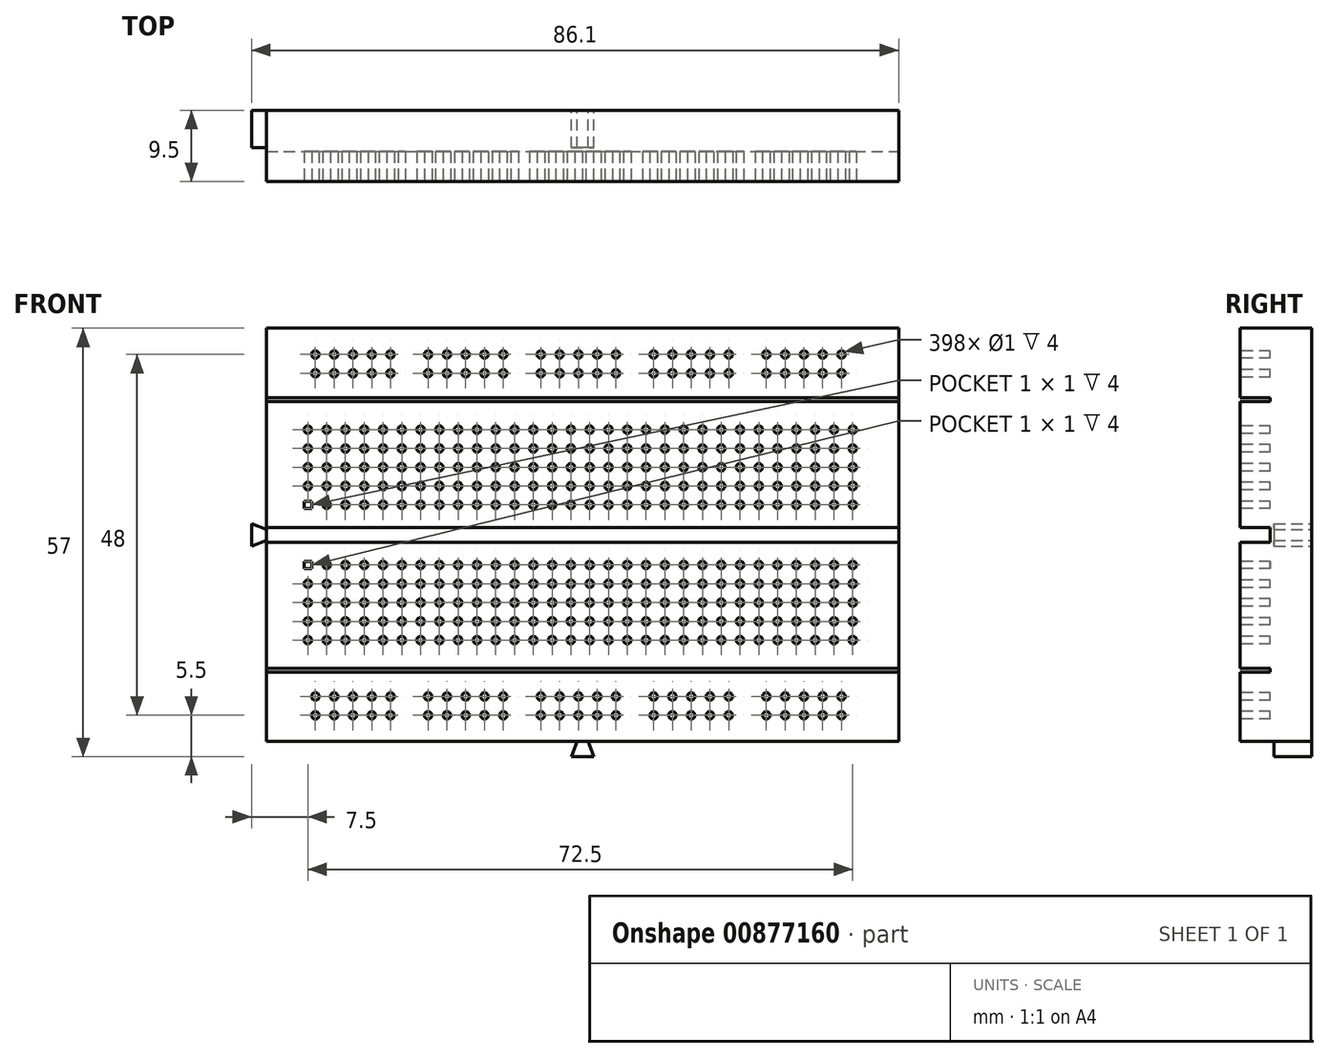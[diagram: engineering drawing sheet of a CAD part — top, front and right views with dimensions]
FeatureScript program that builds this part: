
annotation { "Feature Type Name" : "Feature", "Feature Type Description" : "" }
export const myFeature = defineFeature(function(context is Context, id is Id, definition is map)
    precondition{}
    {
        {
            var Q0;
            Q0=qCreatedBy(makeId("Front.planeOp"),FACE);
            var sketch = newSketch(context, id + "F0", { "sketchPlane" : qUnion([Q0])});
            skLineSegment(sketch, "E0.bottom", {"start": v(42.05, 27.5) * mm, "end": v(-42.05, 27.5) * mm});
            skLineSegment(sketch, "E0.top", {"start": v(42.05, -27.5) * mm, "end": v(-42.05, -27.5) * mm});
            skLineSegment(sketch, "E0.left", {"start": v(42.05, 27.5) * mm, "end": v(42.05, -27.5) * mm});
            skLineSegment(sketch, "E0.right", {"start": v(-42.05, 27.5) * mm, "end": v(-42.05, -27.5) * mm});
            skPoint(sketch, "E0.middle", {"position": v(0, 0) * mm});
            skSolve(sketch);
        }
        {
            var Q0;
            Q0 = qSketchRegion(id + "F0", true);
            extrude(context, id + "F1", {"entities" : qUnion([Q0]), "depth" : 9.5 * mm, "offsetDistance" : 25 * mm});
        }
        {
            var Q0;
            Q0=makeQuery(id+"F1.opExtrude","CAP_FACE",FACE,{"disambiguationData":[OSD([sQuery(id+"F0.wireOp",EDGE,"E0.bottom"),sQuery(id+"F0.wireOp",EDGE,"E0.top"),sQuery(id+"F0.wireOp",EDGE,"E0.left"),sQuery(id+"F0.wireOp",EDGE,"E0.right")])],"isStart":true});
            var sketch = newSketch(context, id + "F2", { "sketchPlane" : qUnion([Q0])});
            skLineSegment(sketch, "E1", {"start": v(42.05, 0.75) * mm, "end": v(44.05, 1.5) * mm});
            skLineSegment(sketch, "E2", {"start": v(44.05, 1.5) * mm, "end": v(44.05, -1.5) * mm});
            skLineSegment(sketch, "E3", {"start": v(44.05, -1.5) * mm, "end": v(42.05, -0.75) * mm});
            skLineSegment(sketch, "E4", {"start": v(0.75, -27.5) * mm, "end": v(1.5, -29.5) * mm});
            skLineSegment(sketch, "E5", {"start": v(1.5, -29.5) * mm, "end": v(-1.5, -29.5) * mm});
            skLineSegment(sketch, "E6", {"start": v(-1.5, -29.5) * mm, "end": v(-0.75, -27.5) * mm});
            skLineSegment(sketch, "E7", {"start": v(42.05, 0) * mm, "end": v(44.05, 0) * mm});
            skLineSegment(sketch, "E8", {"start": v(42.05, 0.75) * mm, "end": v(42.05, -0.75) * mm});
            skLineSegment(sketch, "E9", {"start": v(0.75, -27.5) * mm, "end": v(-0.75, -27.5) * mm});
            skLineSegment(sketch, "E10", {"start": v(0, -27.5) * mm, "end": v(0, -29.5) * mm, "construction": true});
            skSolve(sketch);
        }
        {
            var Q0;
            {var subQ0=sQuery(id+"F2.wireOp",EDGE,"E3");Q0=makeQuery(id+"F2.imprint","IMPRINT",FACE,{"disambiguationData":[TD([[makeQuery(id+"F2.imprint","IMPRINT",EDGE,{"derivedFrom":subQ0}),-1.0]])]});}
            var Q1;
            {var subQ0=sQuery(id+"F2.wireOp",EDGE,"E1");Q1=makeQuery(id+"F2.imprint","IMPRINT",FACE,{"disambiguationData":[TD([[makeQuery(id+"F2.imprint","IMPRINT",EDGE,{"derivedFrom":subQ0}),-1.0]])]});}
            var Q2;
            Q2=makeQuery(id+"F2.imprint","IMPRINT",FACE,{"disambiguationData":[TD([[makeQuery(id+"F2.imprint","IMPRINT",EDGE,{"derivedFrom":sQuery(id+"F2.wireOp",EDGE,"E4")}),-1.0]])]});
            extrude(context, id + "F3", {"entities" : qUnion([Q0, Q1, Q2]), "operationType" : NewBodyOperationType.ADD, "oppositeDirection" : true, "depth" : 5 * mm, "offsetDistance" : 25 * mm});
        }
        {
            var Q0;
            Q0=makeQuery(id+"F1.opExtrude","CAP_FACE",FACE,{"disambiguationData":[OSD([sQuery(id+"F0.wireOp",EDGE,"E0.bottom"),sQuery(id+"F0.wireOp",EDGE,"E0.top"),sQuery(id+"F0.wireOp",EDGE,"E0.left"),sQuery(id+"F0.wireOp",EDGE,"E0.right")])],"isStart":false});
            var sketch = newSketch(context, id + "F4", { "sketchPlane" : qUnion([Q0])});
            skSolve(sketch);
        }
        {
            var Q0;
            Q0=makeQuery(id+"F4.imprint","IMPRINT",FACE,{"disambiguationData":[TD([[makeQuery(id+"F4.imprint","IMPRINT",EDGE,{"derivedFrom":makeQuery(id+"F1.opExtrude","CAP_EDGE",EDGE,{"disambiguationData":[OSD([sQuery(id+"F0.wireOp",EDGE,"E0.bottom")])],"isStart":false})}),1.0]])]});
            var sketch = newSketch(context, id + "F5", { "sketchPlane" : qUnion([Q0])});
            skLineSegment(sketch, "E11.bottom", {"start": v(-42.05, -1) * mm, "end": v(42.05, -1) * mm});
            skLineSegment(sketch, "E11.top", {"start": v(-42.05, 1) * mm, "end": v(42.05, 1) * mm});
            skLineSegment(sketch, "E11.left", {"start": v(-42.05, -1) * mm, "end": v(-42.05, 1) * mm});
            skLineSegment(sketch, "E11.right", {"start": v(42.05, -1) * mm, "end": v(42.05, 1) * mm});
            skPoint(sketch, "E11.middle", {"position": v(0, 0) * mm});
            skLineSegment(sketch, "E12.bottom", {"start": v(-36.05, -3.5) * mm, "end": v(-37.05, -3.5) * mm});
            skLineSegment(sketch, "E12.top", {"start": v(-36.05, -4.5) * mm, "end": v(-37.05, -4.5) * mm});
            skLineSegment(sketch, "E12.left", {"start": v(-36.05, -3.5) * mm, "end": v(-36.05, -4.5) * mm});
            skLineSegment(sketch, "E12.right", {"start": v(-37.05, -3.5) * mm, "end": v(-37.05, -4.5) * mm});
            skPoint(sketch, "E12.middle", {"position": v(-36.55, -4) * mm});
            skCircle(sketch, "E13", {"center": v(-36.55, -4) * mm, "radius": 0.5 * mm});
            skCircle(sketch, "E14.1.0.0", {"center": v(-34.05, -4) * mm, "radius": 0.5 * mm});
            skCircle(sketch, "E14.2.0.0", {"center": v(-31.55, -4) * mm, "radius": 0.5 * mm});
            skCircle(sketch, "E14.3.0.0", {"center": v(-29.05, -4) * mm, "radius": 0.5 * mm});
            skCircle(sketch, "E14.4.0.0", {"center": v(-26.55, -4) * mm, "radius": 0.5 * mm});
            skCircle(sketch, "E14.5.0.0", {"center": v(-24.05, -4) * mm, "radius": 0.5 * mm});
            skCircle(sketch, "E14.6.0.0", {"center": v(-21.55, -4) * mm, "radius": 0.5 * mm});
            skCircle(sketch, "E14.7.0.0", {"center": v(-19.05, -4) * mm, "radius": 0.5 * mm});
            skCircle(sketch, "E14.8.0.0", {"center": v(-16.55, -4) * mm, "radius": 0.5 * mm});
            skCircle(sketch, "E14.9.0.0", {"center": v(-14.05, -4) * mm, "radius": 0.5 * mm});
            skCircle(sketch, "E14.10.0.0", {"center": v(-11.55, -4) * mm, "radius": 0.5 * mm});
            skCircle(sketch, "E14.11.0.0", {"center": v(-9.05, -4) * mm, "radius": 0.5 * mm});
            skCircle(sketch, "E14.12.0.0", {"center": v(-6.55, -4) * mm, "radius": 0.5 * mm});
            skCircle(sketch, "E14.13.0.0", {"center": v(-4.05, -4) * mm, "radius": 0.5 * mm});
            skCircle(sketch, "E14.14.0.0", {"center": v(-1.55, -4) * mm, "radius": 0.5 * mm});
            skCircle(sketch, "E14.15.0.0", {"center": v(0.95, -4) * mm, "radius": 0.5 * mm});
            skCircle(sketch, "E14.16.0.0", {"center": v(3.45, -4) * mm, "radius": 0.5 * mm});
            skCircle(sketch, "E14.17.0.0", {"center": v(5.95, -4) * mm, "radius": 0.5 * mm});
            skCircle(sketch, "E14.18.0.0", {"center": v(8.45, -4) * mm, "radius": 0.5 * mm});
            skCircle(sketch, "E14.19.0.0", {"center": v(10.95, -4) * mm, "radius": 0.5 * mm});
            skCircle(sketch, "E14.20.0.0", {"center": v(13.45, -4) * mm, "radius": 0.5 * mm});
            skCircle(sketch, "E14.21.0.0", {"center": v(15.95, -4) * mm, "radius": 0.5 * mm});
            skCircle(sketch, "E14.22.0.0", {"center": v(18.45, -4) * mm, "radius": 0.5 * mm});
            skCircle(sketch, "E14.23.0.0", {"center": v(20.95, -4) * mm, "radius": 0.5 * mm});
            skCircle(sketch, "E14.24.0.0", {"center": v(23.45, -4) * mm, "radius": 0.5 * mm});
            skCircle(sketch, "E14.25.0.0", {"center": v(25.95, -4) * mm, "radius": 0.5 * mm});
            skCircle(sketch, "E14.26.0.0", {"center": v(28.45, -4) * mm, "radius": 0.5 * mm});
            skCircle(sketch, "E14.27.0.0", {"center": v(30.95, -4) * mm, "radius": 0.5 * mm});
            skCircle(sketch, "E14.28.0.0", {"center": v(33.45, -4) * mm, "radius": 0.5 * mm});
            skCircle(sketch, "E14.29.0.0", {"center": v(35.95, -4) * mm, "radius": 0.5 * mm});
            skLineSegment(sketch, "E14.direction1", {"start": v(-36.55, -4) * mm, "end": v(-34.05, -4) * mm, "construction": true});
            skPoint(sketch, "E15.0.1.0", {"position": v(-36.55, -6.5) * mm});
            skCircle(sketch, "E15.0.1.1", {"center": v(25.95, -6.5) * mm, "radius": 0.5 * mm});
            skCircle(sketch, "E15.0.1.2", {"center": v(28.45, -6.5) * mm, "radius": 0.5 * mm});
            skCircle(sketch, "E15.0.1.3", {"center": v(-16.55, -6.5) * mm, "radius": 0.5 * mm});
            skCircle(sketch, "E15.0.1.4", {"center": v(5.95, -6.5) * mm, "radius": 0.5 * mm});
            skCircle(sketch, "E15.0.1.5", {"center": v(-31.55, -6.5) * mm, "radius": 0.5 * mm});
            skCircle(sketch, "E15.0.1.6", {"center": v(20.95, -6.5) * mm, "radius": 0.5 * mm});
            skCircle(sketch, "E15.0.1.7", {"center": v(-9.05, -6.5) * mm, "radius": 0.5 * mm});
            skCircle(sketch, "E15.0.1.8", {"center": v(10.95, -6.5) * mm, "radius": 0.5 * mm});
            skCircle(sketch, "E15.0.1.9", {"center": v(0.95, -6.5) * mm, "radius": 0.5 * mm});
            skCircle(sketch, "E15.0.1.10", {"center": v(8.45, -6.5) * mm, "radius": 0.5 * mm});
            skCircle(sketch, "E15.0.1.11", {"center": v(-14.05, -6.5) * mm, "radius": 0.5 * mm});
            skCircle(sketch, "E15.0.1.12", {"center": v(-4.05, -6.5) * mm, "radius": 0.5 * mm});
            skCircle(sketch, "E15.0.1.13", {"center": v(-11.55, -6.5) * mm, "radius": 0.5 * mm});
            skCircle(sketch, "E15.0.1.14", {"center": v(15.95, -6.5) * mm, "radius": 0.5 * mm});
            skCircle(sketch, "E15.0.1.15", {"center": v(3.45, -6.5) * mm, "radius": 0.5 * mm});
            skCircle(sketch, "E15.0.1.16", {"center": v(13.45, -6.5) * mm, "radius": 0.5 * mm});
            skCircle(sketch, "E15.0.1.17", {"center": v(-6.55, -6.5) * mm, "radius": 0.5 * mm});
            skCircle(sketch, "E15.0.1.18", {"center": v(-29.05, -6.5) * mm, "radius": 0.5 * mm});
            skCircle(sketch, "E15.0.1.19", {"center": v(18.45, -6.5) * mm, "radius": 0.5 * mm});
            skCircle(sketch, "E15.0.1.20", {"center": v(23.45, -6.5) * mm, "radius": 0.5 * mm});
            skCircle(sketch, "E15.0.1.21", {"center": v(30.95, -6.5) * mm, "radius": 0.5 * mm});
            skCircle(sketch, "E15.0.1.22", {"center": v(33.45, -6.5) * mm, "radius": 0.5 * mm});
            skCircle(sketch, "E15.0.1.23", {"center": v(-21.55, -6.5) * mm, "radius": 0.5 * mm});
            skCircle(sketch, "E15.0.1.24", {"center": v(-26.55, -6.5) * mm, "radius": 0.5 * mm});
            skCircle(sketch, "E15.0.1.25", {"center": v(-24.05, -6.5) * mm, "radius": 0.5 * mm});
            skCircle(sketch, "E15.0.1.26", {"center": v(-19.05, -6.5) * mm, "radius": 0.5 * mm});
            skCircle(sketch, "E15.0.1.27", {"center": v(35.95, -6.5) * mm, "radius": 0.5 * mm});
            skCircle(sketch, "E15.0.1.28", {"center": v(-1.55, -6.5) * mm, "radius": 0.5 * mm});
            skCircle(sketch, "E15.0.1.29", {"center": v(-34.05, -6.5) * mm, "radius": 0.5 * mm});
            skCircle(sketch, "E15.0.1.30", {"center": v(-36.55, -6.5) * mm, "radius": 0.5 * mm});
            skPoint(sketch, "E15.0.2.0", {"position": v(-36.55, -9) * mm});
            skCircle(sketch, "E15.0.2.1", {"center": v(25.95, -9) * mm, "radius": 0.5 * mm});
            skCircle(sketch, "E15.0.2.2", {"center": v(28.45, -9) * mm, "radius": 0.5 * mm});
            skCircle(sketch, "E15.0.2.3", {"center": v(-16.55, -9) * mm, "radius": 0.5 * mm});
            skCircle(sketch, "E15.0.2.4", {"center": v(5.95, -9) * mm, "radius": 0.5 * mm});
            skCircle(sketch, "E15.0.2.5", {"center": v(-31.55, -9) * mm, "radius": 0.5 * mm});
            skCircle(sketch, "E15.0.2.6", {"center": v(20.95, -9) * mm, "radius": 0.5 * mm});
            skCircle(sketch, "E15.0.2.7", {"center": v(-9.05, -9) * mm, "radius": 0.5 * mm});
            skCircle(sketch, "E15.0.2.8", {"center": v(10.95, -9) * mm, "radius": 0.5 * mm});
            skCircle(sketch, "E15.0.2.9", {"center": v(0.95, -9) * mm, "radius": 0.5 * mm});
            skCircle(sketch, "E15.0.2.10", {"center": v(8.45, -9) * mm, "radius": 0.5 * mm});
            skCircle(sketch, "E15.0.2.11", {"center": v(-14.05, -9) * mm, "radius": 0.5 * mm});
            skCircle(sketch, "E15.0.2.12", {"center": v(-4.05, -9) * mm, "radius": 0.5 * mm});
            skCircle(sketch, "E15.0.2.13", {"center": v(-11.55, -9) * mm, "radius": 0.5 * mm});
            skCircle(sketch, "E15.0.2.14", {"center": v(15.95, -9) * mm, "radius": 0.5 * mm});
            skCircle(sketch, "E15.0.2.15", {"center": v(3.45, -9) * mm, "radius": 0.5 * mm});
            skCircle(sketch, "E15.0.2.16", {"center": v(13.45, -9) * mm, "radius": 0.5 * mm});
            skCircle(sketch, "E15.0.2.17", {"center": v(-6.55, -9) * mm, "radius": 0.5 * mm});
            skCircle(sketch, "E15.0.2.18", {"center": v(-29.05, -9) * mm, "radius": 0.5 * mm});
            skCircle(sketch, "E15.0.2.19", {"center": v(18.45, -9) * mm, "radius": 0.5 * mm});
            skCircle(sketch, "E15.0.2.20", {"center": v(23.45, -9) * mm, "radius": 0.5 * mm});
            skCircle(sketch, "E15.0.2.21", {"center": v(30.95, -9) * mm, "radius": 0.5 * mm});
            skCircle(sketch, "E15.0.2.22", {"center": v(33.45, -9) * mm, "radius": 0.5 * mm});
            skCircle(sketch, "E15.0.2.23", {"center": v(-21.55, -9) * mm, "radius": 0.5 * mm});
            skCircle(sketch, "E15.0.2.24", {"center": v(-26.55, -9) * mm, "radius": 0.5 * mm});
            skCircle(sketch, "E15.0.2.25", {"center": v(-24.05, -9) * mm, "radius": 0.5 * mm});
            skCircle(sketch, "E15.0.2.26", {"center": v(-19.05, -9) * mm, "radius": 0.5 * mm});
            skCircle(sketch, "E15.0.2.27", {"center": v(35.95, -9) * mm, "radius": 0.5 * mm});
            skCircle(sketch, "E15.0.2.28", {"center": v(-1.55, -9) * mm, "radius": 0.5 * mm});
            skCircle(sketch, "E15.0.2.29", {"center": v(-34.05, -9) * mm, "radius": 0.5 * mm});
            skCircle(sketch, "E15.0.2.30", {"center": v(-36.55, -9) * mm, "radius": 0.5 * mm});
            skPoint(sketch, "E15.0.3.0", {"position": v(-36.55, -11.5) * mm});
            skCircle(sketch, "E15.0.3.1", {"center": v(25.95, -11.5) * mm, "radius": 0.5 * mm});
            skCircle(sketch, "E15.0.3.2", {"center": v(28.45, -11.5) * mm, "radius": 0.5 * mm});
            skCircle(sketch, "E15.0.3.3", {"center": v(-16.55, -11.5) * mm, "radius": 0.5 * mm});
            skCircle(sketch, "E15.0.3.4", {"center": v(5.95, -11.5) * mm, "radius": 0.5 * mm});
            skCircle(sketch, "E15.0.3.5", {"center": v(-31.55, -11.5) * mm, "radius": 0.5 * mm});
            skCircle(sketch, "E15.0.3.6", {"center": v(20.95, -11.5) * mm, "radius": 0.5 * mm});
            skCircle(sketch, "E15.0.3.7", {"center": v(-9.05, -11.5) * mm, "radius": 0.5 * mm});
            skCircle(sketch, "E15.0.3.8", {"center": v(10.95, -11.5) * mm, "radius": 0.5 * mm});
            skCircle(sketch, "E15.0.3.9", {"center": v(0.95, -11.5) * mm, "radius": 0.5 * mm});
            skCircle(sketch, "E15.0.3.10", {"center": v(8.45, -11.5) * mm, "radius": 0.5 * mm});
            skCircle(sketch, "E15.0.3.11", {"center": v(-14.05, -11.5) * mm, "radius": 0.5 * mm});
            skCircle(sketch, "E15.0.3.12", {"center": v(-4.05, -11.5) * mm, "radius": 0.5 * mm});
            skCircle(sketch, "E15.0.3.13", {"center": v(-11.55, -11.5) * mm, "radius": 0.5 * mm});
            skCircle(sketch, "E15.0.3.14", {"center": v(15.95, -11.5) * mm, "radius": 0.5 * mm});
            skCircle(sketch, "E15.0.3.15", {"center": v(3.45, -11.5) * mm, "radius": 0.5 * mm});
            skCircle(sketch, "E15.0.3.16", {"center": v(13.45, -11.5) * mm, "radius": 0.5 * mm});
            skCircle(sketch, "E15.0.3.17", {"center": v(-6.55, -11.5) * mm, "radius": 0.5 * mm});
            skCircle(sketch, "E15.0.3.18", {"center": v(-29.05, -11.5) * mm, "radius": 0.5 * mm});
            skCircle(sketch, "E15.0.3.19", {"center": v(18.45, -11.5) * mm, "radius": 0.5 * mm});
            skCircle(sketch, "E15.0.3.20", {"center": v(23.45, -11.5) * mm, "radius": 0.5 * mm});
            skCircle(sketch, "E15.0.3.21", {"center": v(30.95, -11.5) * mm, "radius": 0.5 * mm});
            skCircle(sketch, "E15.0.3.22", {"center": v(33.45, -11.5) * mm, "radius": 0.5 * mm});
            skCircle(sketch, "E15.0.3.23", {"center": v(-21.55, -11.5) * mm, "radius": 0.5 * mm});
            skCircle(sketch, "E15.0.3.24", {"center": v(-26.55, -11.5) * mm, "radius": 0.5 * mm});
            skCircle(sketch, "E15.0.3.25", {"center": v(-24.05, -11.5) * mm, "radius": 0.5 * mm});
            skCircle(sketch, "E15.0.3.26", {"center": v(-19.05, -11.5) * mm, "radius": 0.5 * mm});
            skCircle(sketch, "E15.0.3.27", {"center": v(35.95, -11.5) * mm, "radius": 0.5 * mm});
            skCircle(sketch, "E15.0.3.28", {"center": v(-1.55, -11.5) * mm, "radius": 0.5 * mm});
            skCircle(sketch, "E15.0.3.29", {"center": v(-34.05, -11.5) * mm, "radius": 0.5 * mm});
            skCircle(sketch, "E15.0.3.30", {"center": v(-36.55, -11.5) * mm, "radius": 0.5 * mm});
            skPoint(sketch, "E15.0.4.0", {"position": v(-36.55, -14) * mm});
            skCircle(sketch, "E15.0.4.1", {"center": v(25.95, -14) * mm, "radius": 0.5 * mm});
            skCircle(sketch, "E15.0.4.2", {"center": v(28.45, -14) * mm, "radius": 0.5 * mm});
            skCircle(sketch, "E15.0.4.3", {"center": v(-16.55, -14) * mm, "radius": 0.5 * mm});
            skCircle(sketch, "E15.0.4.4", {"center": v(5.95, -14) * mm, "radius": 0.5 * mm});
            skCircle(sketch, "E15.0.4.5", {"center": v(-31.55, -14) * mm, "radius": 0.5 * mm});
            skCircle(sketch, "E15.0.4.6", {"center": v(20.95, -14) * mm, "radius": 0.5 * mm});
            skCircle(sketch, "E15.0.4.7", {"center": v(-9.05, -14) * mm, "radius": 0.5 * mm});
            skCircle(sketch, "E15.0.4.8", {"center": v(10.95, -14) * mm, "radius": 0.5 * mm});
            skCircle(sketch, "E15.0.4.9", {"center": v(0.95, -14) * mm, "radius": 0.5 * mm});
            skCircle(sketch, "E15.0.4.10", {"center": v(8.45, -14) * mm, "radius": 0.5 * mm});
            skCircle(sketch, "E15.0.4.11", {"center": v(-14.05, -14) * mm, "radius": 0.5 * mm});
            skCircle(sketch, "E15.0.4.12", {"center": v(-4.05, -14) * mm, "radius": 0.5 * mm});
            skCircle(sketch, "E15.0.4.13", {"center": v(-11.55, -14) * mm, "radius": 0.5 * mm});
            skCircle(sketch, "E15.0.4.14", {"center": v(15.95, -14) * mm, "radius": 0.5 * mm});
            skCircle(sketch, "E15.0.4.15", {"center": v(3.45, -14) * mm, "radius": 0.5 * mm});
            skCircle(sketch, "E15.0.4.16", {"center": v(13.45, -14) * mm, "radius": 0.5 * mm});
            skCircle(sketch, "E15.0.4.17", {"center": v(-6.55, -14) * mm, "radius": 0.5 * mm});
            skCircle(sketch, "E15.0.4.18", {"center": v(-29.05, -14) * mm, "radius": 0.5 * mm});
            skCircle(sketch, "E15.0.4.19", {"center": v(18.45, -14) * mm, "radius": 0.5 * mm});
            skCircle(sketch, "E15.0.4.20", {"center": v(23.45, -14) * mm, "radius": 0.5 * mm});
            skCircle(sketch, "E15.0.4.21", {"center": v(30.95, -14) * mm, "radius": 0.5 * mm});
            skCircle(sketch, "E15.0.4.22", {"center": v(33.45, -14) * mm, "radius": 0.5 * mm});
            skCircle(sketch, "E15.0.4.23", {"center": v(-21.55, -14) * mm, "radius": 0.5 * mm});
            skCircle(sketch, "E15.0.4.24", {"center": v(-26.55, -14) * mm, "radius": 0.5 * mm});
            skCircle(sketch, "E15.0.4.25", {"center": v(-24.05, -14) * mm, "radius": 0.5 * mm});
            skCircle(sketch, "E15.0.4.26", {"center": v(-19.05, -14) * mm, "radius": 0.5 * mm});
            skCircle(sketch, "E15.0.4.27", {"center": v(35.95, -14) * mm, "radius": 0.5 * mm});
            skCircle(sketch, "E15.0.4.28", {"center": v(-1.55, -14) * mm, "radius": 0.5 * mm});
            skCircle(sketch, "E15.0.4.29", {"center": v(-34.05, -14) * mm, "radius": 0.5 * mm});
            skCircle(sketch, "E15.0.4.30", {"center": v(-36.55, -14) * mm, "radius": 0.5 * mm});
            skLineSegment(sketch, "E15.direction1", {"start": v(-36.55, -4) * mm, "end": v(-11.55, -4) * mm, "construction": true});
            skLineSegment(sketch, "E15.direction2", {"start": v(-36.55, -4) * mm, "end": v(-36.55, -6.5) * mm, "construction": true});
            skLineSegment(sketch, "E16.bottom", {"start": v(-42.05, -17.75) * mm, "end": v(42.05, -17.75) * mm});
            skLineSegment(sketch, "E16.top", {"start": v(-42.05, -18.25) * mm, "end": v(42.05, -18.25) * mm});
            skLineSegment(sketch, "E16.left", {"start": v(-42.05, -17.75) * mm, "end": v(-42.05, -18.25) * mm});
            skLineSegment(sketch, "E16.right", {"start": v(42.05, -17.75) * mm, "end": v(42.05, -18.25) * mm});
            skCircle(sketch, "E17.0.4.30", {"center": v(-35.55, -21.5) * mm, "radius": 0.5 * mm});
            skCircle(sketch, "E18.0.1.0", {"center": v(-35.55, -24) * mm, "radius": 0.5 * mm});
            skCircle(sketch, "E18.1.0.0", {"center": v(-33.05, -21.5) * mm, "radius": 0.5 * mm});
            skCircle(sketch, "E18.1.1.0", {"center": v(-33.05, -24) * mm, "radius": 0.5 * mm});
            skCircle(sketch, "E18.2.0.0", {"center": v(-30.55, -21.5) * mm, "radius": 0.5 * mm});
            skCircle(sketch, "E18.2.1.0", {"center": v(-30.55, -24) * mm, "radius": 0.5 * mm});
            skCircle(sketch, "E18.3.0.0", {"center": v(-28.05, -21.5) * mm, "radius": 0.5 * mm});
            skCircle(sketch, "E18.3.1.0", {"center": v(-28.05, -24) * mm, "radius": 0.5 * mm});
            skCircle(sketch, "E18.4.0.0", {"center": v(-25.55, -21.5) * mm, "radius": 0.5 * mm});
            skCircle(sketch, "E18.4.1.0", {"center": v(-25.55, -24) * mm, "radius": 0.5 * mm});
            skLineSegment(sketch, "E18.direction1", {"start": v(-35.55, -21.5) * mm, "end": v(-33.05, -21.5) * mm, "construction": true});
            skLineSegment(sketch, "E18.direction2", {"start": v(-35.55, -21.5) * mm, "end": v(-35.55, -24) * mm, "construction": true});
            skCircle(sketch, "E19.1.0.0", {"center": v(-18.05, -24) * mm, "radius": 0.5 * mm});
            skCircle(sketch, "E19.1.0.1", {"center": v(-10.55, -24) * mm, "radius": 0.5 * mm});
            skCircle(sketch, "E19.1.0.2", {"center": v(-13.05, -21.5) * mm, "radius": 0.5 * mm});
            skCircle(sketch, "E19.1.0.3", {"center": v(-18.05, -21.5) * mm, "radius": 0.5 * mm});
            skCircle(sketch, "E19.1.0.4", {"center": v(-15.55, -21.5) * mm, "radius": 0.5 * mm});
            skLineSegment(sketch, "E19.1.0.5", {"start": v(-20.55, -21.5) * mm, "end": v(-18.05, -21.5) * mm, "construction": true});
            skLineSegment(sketch, "E19.1.0.6", {"start": v(-20.55, -21.5) * mm, "end": v(-20.55, -24) * mm, "construction": true});
            skCircle(sketch, "E19.1.0.7", {"center": v(-20.55, -24) * mm, "radius": 0.5 * mm});
            skCircle(sketch, "E19.1.0.8", {"center": v(-13.05, -24) * mm, "radius": 0.5 * mm});
            skCircle(sketch, "E19.1.0.9", {"center": v(-10.55, -21.5) * mm, "radius": 0.5 * mm});
            skCircle(sketch, "E19.1.0.10", {"center": v(-15.55, -24) * mm, "radius": 0.5 * mm});
            skCircle(sketch, "E19.1.0.11", {"center": v(-20.55, -21.5) * mm, "radius": 0.5 * mm});
            skCircle(sketch, "E19.2.0.0", {"center": v(-3.05, -24) * mm, "radius": 0.5 * mm});
            skCircle(sketch, "E19.2.0.1", {"center": v(4.45, -24) * mm, "radius": 0.5 * mm});
            skCircle(sketch, "E19.2.0.2", {"center": v(1.95, -21.5) * mm, "radius": 0.5 * mm});
            skCircle(sketch, "E19.2.0.3", {"center": v(-3.05, -21.5) * mm, "radius": 0.5 * mm});
            skCircle(sketch, "E19.2.0.4", {"center": v(-0.55, -21.5) * mm, "radius": 0.5 * mm});
            skLineSegment(sketch, "E19.2.0.5", {"start": v(-5.55, -21.5) * mm, "end": v(-3.05, -21.5) * mm, "construction": true});
            skLineSegment(sketch, "E19.2.0.6", {"start": v(-5.55, -21.5) * mm, "end": v(-5.55, -24) * mm, "construction": true});
            skCircle(sketch, "E19.2.0.7", {"center": v(-5.55, -24) * mm, "radius": 0.5 * mm});
            skCircle(sketch, "E19.2.0.8", {"center": v(1.95, -24) * mm, "radius": 0.5 * mm});
            skCircle(sketch, "E19.2.0.9", {"center": v(4.45, -21.5) * mm, "radius": 0.5 * mm});
            skCircle(sketch, "E19.2.0.10", {"center": v(-0.55, -24) * mm, "radius": 0.5 * mm});
            skCircle(sketch, "E19.2.0.11", {"center": v(-5.55, -21.5) * mm, "radius": 0.5 * mm});
            skCircle(sketch, "E19.3.0.0", {"center": v(11.95, -24) * mm, "radius": 0.5 * mm});
            skCircle(sketch, "E19.3.0.1", {"center": v(19.45, -24) * mm, "radius": 0.5 * mm});
            skCircle(sketch, "E19.3.0.2", {"center": v(16.95, -21.5) * mm, "radius": 0.5 * mm});
            skCircle(sketch, "E19.3.0.3", {"center": v(11.95, -21.5) * mm, "radius": 0.5 * mm});
            skCircle(sketch, "E19.3.0.4", {"center": v(14.45, -21.5) * mm, "radius": 0.5 * mm});
            skLineSegment(sketch, "E19.3.0.5", {"start": v(9.45, -21.5) * mm, "end": v(11.95, -21.5) * mm, "construction": true});
            skLineSegment(sketch, "E19.3.0.6", {"start": v(9.45, -21.5) * mm, "end": v(9.45, -24) * mm, "construction": true});
            skCircle(sketch, "E19.3.0.7", {"center": v(9.45, -24) * mm, "radius": 0.5 * mm});
            skCircle(sketch, "E19.3.0.8", {"center": v(16.95, -24) * mm, "radius": 0.5 * mm});
            skCircle(sketch, "E19.3.0.9", {"center": v(19.45, -21.5) * mm, "radius": 0.5 * mm});
            skCircle(sketch, "E19.3.0.10", {"center": v(14.45, -24) * mm, "radius": 0.5 * mm});
            skCircle(sketch, "E19.3.0.11", {"center": v(9.45, -21.5) * mm, "radius": 0.5 * mm});
            skCircle(sketch, "E19.4.0.0", {"center": v(26.95, -24) * mm, "radius": 0.5 * mm});
            skCircle(sketch, "E19.4.0.1", {"center": v(34.45, -24) * mm, "radius": 0.5 * mm});
            skCircle(sketch, "E19.4.0.2", {"center": v(31.95, -21.5) * mm, "radius": 0.5 * mm});
            skCircle(sketch, "E19.4.0.3", {"center": v(26.95, -21.5) * mm, "radius": 0.5 * mm});
            skCircle(sketch, "E19.4.0.4", {"center": v(29.45, -21.5) * mm, "radius": 0.5 * mm});
            skLineSegment(sketch, "E19.4.0.5", {"start": v(24.45, -21.5) * mm, "end": v(26.95, -21.5) * mm, "construction": true});
            skLineSegment(sketch, "E19.4.0.6", {"start": v(24.45, -21.5) * mm, "end": v(24.45, -24) * mm, "construction": true});
            skCircle(sketch, "E19.4.0.7", {"center": v(24.45, -24) * mm, "radius": 0.5 * mm});
            skCircle(sketch, "E19.4.0.8", {"center": v(31.95, -24) * mm, "radius": 0.5 * mm});
            skCircle(sketch, "E19.4.0.9", {"center": v(34.45, -21.5) * mm, "radius": 0.5 * mm});
            skCircle(sketch, "E19.4.0.10", {"center": v(29.45, -24) * mm, "radius": 0.5 * mm});
            skCircle(sketch, "E19.4.0.11", {"center": v(24.45, -21.5) * mm, "radius": 0.5 * mm});
            skLineSegment(sketch, "E19.direction1", {"start": v(-35.55, -24) * mm, "end": v(-20.55, -24) * mm, "construction": true});
            skLineSegment(sketch, "E20.MirrorCS", {"start": v(-36.05, 3.5) * mm, "end": v(-37.05, 3.5) * mm});
            skLineSegment(sketch, "E21.MirrorCS", {"start": v(-37.05, 3.5) * mm, "end": v(-37.05, 4.5) * mm});
            skLineSegment(sketch, "E22.MirrorCS", {"start": v(-36.05, 3.5) * mm, "end": v(-36.05, 4.5) * mm});
            skLineSegment(sketch, "E23.MirrorCS", {"start": v(-36.05, 4.5) * mm, "end": v(-37.05, 4.5) * mm});
            skCircle(sketch, "E24.MirrorC", {"center": v(-36.55, 4) * mm, "radius": 0.5 * mm});
            skLineSegment(sketch, "E25.MirrorCS", {"start": v(-36.55, 4) * mm, "end": v(-36.55, 6.5) * mm, "construction": true});
            skCircle(sketch, "E26.MirrorC", {"center": v(-35.55, 21.5) * mm, "radius": 0.5 * mm});
            skCircle(sketch, "E27.MirrorC", {"center": v(24.45, 21.5) * mm, "radius": 0.5 * mm});
            skCircle(sketch, "E28.MirrorC", {"center": v(-20.55, 21.5) * mm, "radius": 0.5 * mm});
            skCircle(sketch, "E29.MirrorC", {"center": v(-36.55, 6.5) * mm, "radius": 0.5 * mm});
            skCircle(sketch, "E30.MirrorC", {"center": v(-5.55, 21.5) * mm, "radius": 0.5 * mm});
            skCircle(sketch, "E31.MirrorC", {"center": v(9.45, 21.5) * mm, "radius": 0.5 * mm});
            skCircle(sketch, "E32.MirrorC", {"center": v(-20.55, 24) * mm, "radius": 0.5 * mm});
            skCircle(sketch, "E33.MirrorC", {"center": v(-35.55, 24) * mm, "radius": 0.5 * mm});
            skLineSegment(sketch, "E34.MirrorCS", {"start": v(-36.55, 4) * mm, "end": v(-34.05, 4) * mm, "construction": true});
            skCircle(sketch, "E35.MirrorC", {"center": v(-36.55, 11.5) * mm, "radius": 0.5 * mm});
            skCircle(sketch, "E36.MirrorC", {"center": v(-3.05, 21.5) * mm, "radius": 0.5 * mm});
            skCircle(sketch, "E37.MirrorC", {"center": v(-5.55, 24) * mm, "radius": 0.5 * mm});
            skCircle(sketch, "E38.MirrorC", {"center": v(-36.55, 9) * mm, "radius": 0.5 * mm});
            skCircle(sketch, "E39.MirrorC", {"center": v(26.95, 21.5) * mm, "radius": 0.5 * mm});
            skCircle(sketch, "E40.MirrorC", {"center": v(-11.55, 4) * mm, "radius": 0.5 * mm});
            skLineSegment(sketch, "E41.MirrorCS", {"start": v(42.05, 17.75) * mm, "end": v(42.05, 18.25) * mm});
            skCircle(sketch, "E42.MirrorC", {"center": v(11.95, 21.5) * mm, "radius": 0.5 * mm});
            skCircle(sketch, "E43.MirrorC", {"center": v(-18.05, 21.5) * mm, "radius": 0.5 * mm});
            skCircle(sketch, "E44.MirrorC", {"center": v(-34.05, 4) * mm, "radius": 0.5 * mm});
            skLineSegment(sketch, "E45.MirrorCS", {"start": v(-42.05, 17.75) * mm, "end": v(-42.05, 18.25) * mm});
            skCircle(sketch, "E46.MirrorC", {"center": v(-36.55, 14) * mm, "radius": 0.5 * mm});
            skCircle(sketch, "E47.MirrorC", {"center": v(9.45, 24) * mm, "radius": 0.5 * mm});
            skCircle(sketch, "E48.MirrorC", {"center": v(24.45, 24) * mm, "radius": 0.5 * mm});
            skCircle(sketch, "E49.MirrorC", {"center": v(-33.05, 21.5) * mm, "radius": 0.5 * mm});
            skCircle(sketch, "E50.MirrorC", {"center": v(-18.05, 24) * mm, "radius": 0.5 * mm});
            skCircle(sketch, "E51.MirrorC", {"center": v(3.45, 4) * mm, "radius": 0.5 * mm});
            skCircle(sketch, "E52.MirrorC", {"center": v(-26.55, 9) * mm, "radius": 0.5 * mm});
            skCircle(sketch, "E53.MirrorC", {"center": v(20.95, 11.5) * mm, "radius": 0.5 * mm});
            skCircle(sketch, "E54.MirrorC", {"center": v(-26.55, 6.5) * mm, "radius": 0.5 * mm});
            skCircle(sketch, "E55.MirrorC", {"center": v(-29.05, 6.5) * mm, "radius": 0.5 * mm});
            skCircle(sketch, "E56.MirrorC", {"center": v(25.95, 11.5) * mm, "radius": 0.5 * mm});
            skCircle(sketch, "E57.MirrorC", {"center": v(30.95, 9) * mm, "radius": 0.5 * mm});
            skCircle(sketch, "E58.MirrorC", {"center": v(-10.55, 24) * mm, "radius": 0.5 * mm});
            skCircle(sketch, "E59.MirrorC", {"center": v(-21.55, 9) * mm, "radius": 0.5 * mm});
            skCircle(sketch, "E60.MirrorC", {"center": v(35.95, 9) * mm, "radius": 0.5 * mm});
            skCircle(sketch, "E61.MirrorC", {"center": v(-21.55, 14) * mm, "radius": 0.5 * mm});
            skCircle(sketch, "E62.MirrorC", {"center": v(16.95, 21.5) * mm, "radius": 0.5 * mm});
            skCircle(sketch, "E63.MirrorC", {"center": v(30.95, 4) * mm, "radius": 0.5 * mm});
            skCircle(sketch, "E64.MirrorC", {"center": v(-11.55, 6.5) * mm, "radius": 0.5 * mm});
            skCircle(sketch, "E65.MirrorC", {"center": v(-19.05, 6.5) * mm, "radius": 0.5 * mm});
            skCircle(sketch, "E66.MirrorC", {"center": v(-9.05, 4) * mm, "radius": 0.5 * mm});
            skCircle(sketch, "E67.MirrorC", {"center": v(25.95, 9) * mm, "radius": 0.5 * mm});
            skCircle(sketch, "E68.MirrorC", {"center": v(-28.05, 24) * mm, "radius": 0.5 * mm});
            skCircle(sketch, "E69.MirrorC", {"center": v(-31.55, 14) * mm, "radius": 0.5 * mm});
            skCircle(sketch, "E70.MirrorC", {"center": v(-19.05, 14) * mm, "radius": 0.5 * mm});
            skCircle(sketch, "E71.MirrorC", {"center": v(-4.05, 4) * mm, "radius": 0.5 * mm});
            skCircle(sketch, "E72.MirrorC", {"center": v(-14.05, 11.5) * mm, "radius": 0.5 * mm});
            skCircle(sketch, "E73.MirrorC", {"center": v(-24.05, 9) * mm, "radius": 0.5 * mm});
            skCircle(sketch, "E74.MirrorC", {"center": v(29.45, 21.5) * mm, "radius": 0.5 * mm});
            skCircle(sketch, "E75.MirrorC", {"center": v(-31.55, 6.5) * mm, "radius": 0.5 * mm});
            skCircle(sketch, "E76.MirrorC", {"center": v(-33.05, 24) * mm, "radius": 0.5 * mm});
            skCircle(sketch, "E77.MirrorC", {"center": v(25.95, 14) * mm, "radius": 0.5 * mm});
            skCircle(sketch, "E78.MirrorC", {"center": v(-1.55, 14) * mm, "radius": 0.5 * mm});
            skCircle(sketch, "E79.MirrorC", {"center": v(-24.05, 4) * mm, "radius": 0.5 * mm});
            skCircle(sketch, "E80.MirrorC", {"center": v(-19.05, 4) * mm, "radius": 0.5 * mm});
            skCircle(sketch, "E81.MirrorC", {"center": v(5.95, 14) * mm, "radius": 0.5 * mm});
            skCircle(sketch, "E82.MirrorC", {"center": v(-14.05, 9) * mm, "radius": 0.5 * mm});
            skCircle(sketch, "E83.MirrorC", {"center": v(-1.55, 11.5) * mm, "radius": 0.5 * mm});
            skCircle(sketch, "E84.MirrorC", {"center": v(-16.55, 14) * mm, "radius": 0.5 * mm});
            skCircle(sketch, "E85.MirrorC", {"center": v(-26.55, 4) * mm, "radius": 0.5 * mm});
            skCircle(sketch, "E86.MirrorC", {"center": v(-29.05, 4) * mm, "radius": 0.5 * mm});
            skCircle(sketch, "E87.MirrorC", {"center": v(33.45, 6.5) * mm, "radius": 0.5 * mm});
            skCircle(sketch, "E88.MirrorC", {"center": v(3.45, 6.5) * mm, "radius": 0.5 * mm});
            skCircle(sketch, "E89.MirrorC", {"center": v(-25.55, 24) * mm, "radius": 0.5 * mm});
            skCircle(sketch, "E90.MirrorC", {"center": v(3.45, 14) * mm, "radius": 0.5 * mm});
            skCircle(sketch, "E91.MirrorC", {"center": v(13.45, 6.5) * mm, "radius": 0.5 * mm});
            skCircle(sketch, "E92.MirrorC", {"center": v(-24.05, 11.5) * mm, "radius": 0.5 * mm});
            skCircle(sketch, "E93.MirrorC", {"center": v(-30.55, 24) * mm, "radius": 0.5 * mm});
            skCircle(sketch, "E94.MirrorC", {"center": v(28.45, 6.5) * mm, "radius": 0.5 * mm});
            skCircle(sketch, "E95.MirrorC", {"center": v(23.45, 9) * mm, "radius": 0.5 * mm});
            skCircle(sketch, "E96.MirrorC", {"center": v(-26.55, 11.5) * mm, "radius": 0.5 * mm});
            skCircle(sketch, "E97.MirrorC", {"center": v(5.95, 9) * mm, "radius": 0.5 * mm});
            skCircle(sketch, "E98.MirrorC", {"center": v(10.95, 14) * mm, "radius": 0.5 * mm});
            skCircle(sketch, "E99.MirrorC", {"center": v(29.45, 24) * mm, "radius": 0.5 * mm});
            skCircle(sketch, "E100.MirrorC", {"center": v(15.95, 9) * mm, "radius": 0.5 * mm});
            skCircle(sketch, "E101.MirrorC", {"center": v(13.45, 4) * mm, "radius": 0.5 * mm});
            skCircle(sketch, "E102.MirrorC", {"center": v(-6.55, 11.5) * mm, "radius": 0.5 * mm});
            skCircle(sketch, "E103.MirrorC", {"center": v(0.95, 14) * mm, "radius": 0.5 * mm});
            skCircle(sketch, "E104.MirrorC", {"center": v(-31.55, 4) * mm, "radius": 0.5 * mm});
            skCircle(sketch, "E105.MirrorC", {"center": v(-29.05, 9) * mm, "radius": 0.5 * mm});
            skCircle(sketch, "E106.MirrorC", {"center": v(-13.05, 21.5) * mm, "radius": 0.5 * mm});
            skCircle(sketch, "E107.MirrorC", {"center": v(35.95, 6.5) * mm, "radius": 0.5 * mm});
            skCircle(sketch, "E108.MirrorC", {"center": v(30.95, 11.5) * mm, "radius": 0.5 * mm});
            skCircle(sketch, "E109.MirrorC", {"center": v(-21.55, 4) * mm, "radius": 0.5 * mm});
            skCircle(sketch, "E110.MirrorC", {"center": v(-24.05, 6.5) * mm, "radius": 0.5 * mm});
            skCircle(sketch, "E111.MirrorC", {"center": v(8.45, 11.5) * mm, "radius": 0.5 * mm});
            skCircle(sketch, "E112.MirrorC", {"center": v(-16.55, 4) * mm, "radius": 0.5 * mm});
            skCircle(sketch, "E113.MirrorC", {"center": v(13.45, 9) * mm, "radius": 0.5 * mm});
            skCircle(sketch, "E114.MirrorC", {"center": v(-4.05, 6.5) * mm, "radius": 0.5 * mm});
            skCircle(sketch, "E115.MirrorC", {"center": v(15.95, 11.5) * mm, "radius": 0.5 * mm});
            skCircle(sketch, "E116.MirrorC", {"center": v(-6.55, 4) * mm, "radius": 0.5 * mm});
            skCircle(sketch, "E117.MirrorC", {"center": v(-6.55, 6.5) * mm, "radius": 0.5 * mm});
            skCircle(sketch, "E118.MirrorC", {"center": v(-16.55, 9) * mm, "radius": 0.5 * mm});
            skCircle(sketch, "E119.MirrorC", {"center": v(-4.05, 11.5) * mm, "radius": 0.5 * mm});
            skCircle(sketch, "E120.MirrorC", {"center": v(18.45, 14) * mm, "radius": 0.5 * mm});
            skCircle(sketch, "E121.MirrorC", {"center": v(5.95, 6.5) * mm, "radius": 0.5 * mm});
            skCircle(sketch, "E122.MirrorC", {"center": v(19.45, 21.5) * mm, "radius": 0.5 * mm});
            skCircle(sketch, "E123.MirrorC", {"center": v(0.95, 11.5) * mm, "radius": 0.5 * mm});
            skCircle(sketch, "E124.MirrorC", {"center": v(-1.55, 4) * mm, "radius": 0.5 * mm});
            skCircle(sketch, "E125.MirrorC", {"center": v(-4.05, 14) * mm, "radius": 0.5 * mm});
            skCircle(sketch, "E126.MirrorC", {"center": v(31.95, 24) * mm, "radius": 0.5 * mm});
            skCircle(sketch, "E127.MirrorC", {"center": v(-26.55, 14) * mm, "radius": 0.5 * mm});
            skCircle(sketch, "E128.MirrorC", {"center": v(10.95, 11.5) * mm, "radius": 0.5 * mm});
            skCircle(sketch, "E129.MirrorC", {"center": v(-1.55, 6.5) * mm, "radius": 0.5 * mm});
            skCircle(sketch, "E130.MirrorC", {"center": v(15.95, 14) * mm, "radius": 0.5 * mm});
            skCircle(sketch, "E131.MirrorC", {"center": v(-10.55, 21.5) * mm, "radius": 0.5 * mm});
            skCircle(sketch, "E132.MirrorC", {"center": v(5.95, 11.5) * mm, "radius": 0.5 * mm});
            skCircle(sketch, "E133.MirrorC", {"center": v(15.95, 6.5) * mm, "radius": 0.5 * mm});
            skCircle(sketch, "E134.MirrorC", {"center": v(-0.55, 24) * mm, "radius": 0.5 * mm});
            skCircle(sketch, "E135.MirrorC", {"center": v(33.45, 11.5) * mm, "radius": 0.5 * mm});
            skCircle(sketch, "E136.MirrorC", {"center": v(28.45, 11.5) * mm, "radius": 0.5 * mm});
            skCircle(sketch, "E137.MirrorC", {"center": v(-0.55, 21.5) * mm, "radius": 0.5 * mm});
            skCircle(sketch, "E138.MirrorC", {"center": v(0.95, 4) * mm, "radius": 0.5 * mm});
            skCircle(sketch, "E139.MirrorC", {"center": v(8.45, 4) * mm, "radius": 0.5 * mm});
            skCircle(sketch, "E140.MirrorC", {"center": v(25.95, 6.5) * mm, "radius": 0.5 * mm});
            skCircle(sketch, "E141.MirrorC", {"center": v(-11.55, 11.5) * mm, "radius": 0.5 * mm});
            skCircle(sketch, "E142.MirrorC", {"center": v(-28.05, 21.5) * mm, "radius": 0.5 * mm});
            skCircle(sketch, "E143.MirrorC", {"center": v(-9.05, 11.5) * mm, "radius": 0.5 * mm});
            skCircle(sketch, "E144.MirrorC", {"center": v(13.45, 11.5) * mm, "radius": 0.5 * mm});
            skCircle(sketch, "E145.MirrorC", {"center": v(20.95, 14) * mm, "radius": 0.5 * mm});
            skCircle(sketch, "E146.MirrorC", {"center": v(8.45, 6.5) * mm, "radius": 0.5 * mm});
            skCircle(sketch, "E147.MirrorC", {"center": v(-24.05, 14) * mm, "radius": 0.5 * mm});
            skCircle(sketch, "E148.MirrorC", {"center": v(-6.55, 14) * mm, "radius": 0.5 * mm});
            skCircle(sketch, "E149.MirrorC", {"center": v(-30.55, 21.5) * mm, "radius": 0.5 * mm});
            skCircle(sketch, "E150.MirrorC", {"center": v(23.45, 4) * mm, "radius": 0.5 * mm});
            skCircle(sketch, "E151.MirrorC", {"center": v(19.45, 24) * mm, "radius": 0.5 * mm});
            skCircle(sketch, "E152.MirrorC", {"center": v(-11.55, 14) * mm, "radius": 0.5 * mm});
            skCircle(sketch, "E153.MirrorC", {"center": v(18.45, 9) * mm, "radius": 0.5 * mm});
            skCircle(sketch, "E154.MirrorC", {"center": v(-34.05, 11.5) * mm, "radius": 0.5 * mm});
            skCircle(sketch, "E155.MirrorC", {"center": v(28.45, 14) * mm, "radius": 0.5 * mm});
            skCircle(sketch, "E156.MirrorC", {"center": v(35.95, 14) * mm, "radius": 0.5 * mm});
            skCircle(sketch, "E157.MirrorC", {"center": v(35.95, 4) * mm, "radius": 0.5 * mm});
            skCircle(sketch, "E158.MirrorC", {"center": v(-4.05, 9) * mm, "radius": 0.5 * mm});
            skCircle(sketch, "E159.MirrorC", {"center": v(33.45, 9) * mm, "radius": 0.5 * mm});
            skCircle(sketch, "E160.MirrorC", {"center": v(20.95, 9) * mm, "radius": 0.5 * mm});
            skCircle(sketch, "E161.MirrorC", {"center": v(33.45, 14) * mm, "radius": 0.5 * mm});
            skCircle(sketch, "E162.MirrorC", {"center": v(34.45, 24) * mm, "radius": 0.5 * mm});
            skCircle(sketch, "E163.MirrorC", {"center": v(35.95, 11.5) * mm, "radius": 0.5 * mm});
            skCircle(sketch, "E164.MirrorC", {"center": v(14.45, 24) * mm, "radius": 0.5 * mm});
            skCircle(sketch, "E165.MirrorC", {"center": v(-31.55, 9) * mm, "radius": 0.5 * mm});
            skCircle(sketch, "E166.MirrorC", {"center": v(0.95, 9) * mm, "radius": 0.5 * mm});
            skCircle(sketch, "E167.MirrorC", {"center": v(18.45, 11.5) * mm, "radius": 0.5 * mm});
            skCircle(sketch, "E168.MirrorC", {"center": v(-13.05, 24) * mm, "radius": 0.5 * mm});
            skCircle(sketch, "E169.MirrorC", {"center": v(4.45, 21.5) * mm, "radius": 0.5 * mm});
            skCircle(sketch, "E170.MirrorC", {"center": v(28.45, 9) * mm, "radius": 0.5 * mm});
            skCircle(sketch, "E171.MirrorC", {"center": v(8.45, 14) * mm, "radius": 0.5 * mm});
            skCircle(sketch, "E172.MirrorC", {"center": v(1.95, 21.5) * mm, "radius": 0.5 * mm});
            skCircle(sketch, "E173.MirrorC", {"center": v(-21.55, 6.5) * mm, "radius": 0.5 * mm});
            skCircle(sketch, "E174.MirrorC", {"center": v(3.45, 11.5) * mm, "radius": 0.5 * mm});
            skCircle(sketch, "E175.MirrorC", {"center": v(-9.05, 9) * mm, "radius": 0.5 * mm});
            skCircle(sketch, "E176.MirrorC", {"center": v(-19.05, 9) * mm, "radius": 0.5 * mm});
            skCircle(sketch, "E177.MirrorC", {"center": v(-16.55, 11.5) * mm, "radius": 0.5 * mm});
            skCircle(sketch, "E178.MirrorC", {"center": v(5.95, 4) * mm, "radius": 0.5 * mm});
            skCircle(sketch, "E179.MirrorC", {"center": v(-34.05, 14) * mm, "radius": 0.5 * mm});
            skCircle(sketch, "E180.MirrorC", {"center": v(18.45, 4) * mm, "radius": 0.5 * mm});
            skCircle(sketch, "E181.MirrorC", {"center": v(-9.05, 14) * mm, "radius": 0.5 * mm});
            skCircle(sketch, "E182.MirrorC", {"center": v(-19.05, 11.5) * mm, "radius": 0.5 * mm});
            skCircle(sketch, "E183.MirrorC", {"center": v(-1.55, 9) * mm, "radius": 0.5 * mm});
            skCircle(sketch, "E184.MirrorC", {"center": v(-34.05, 9) * mm, "radius": 0.5 * mm});
            skCircle(sketch, "E185.MirrorC", {"center": v(23.45, 6.5) * mm, "radius": 0.5 * mm});
            skCircle(sketch, "E186.MirrorC", {"center": v(30.95, 14) * mm, "radius": 0.5 * mm});
            skCircle(sketch, "E187.MirrorC", {"center": v(-6.55, 9) * mm, "radius": 0.5 * mm});
            skCircle(sketch, "E188.MirrorC", {"center": v(13.45, 14) * mm, "radius": 0.5 * mm});
            skCircle(sketch, "E189.MirrorC", {"center": v(-34.05, 6.5) * mm, "radius": 0.5 * mm});
            skCircle(sketch, "E190.MirrorC", {"center": v(16.95, 24) * mm, "radius": 0.5 * mm});
            skCircle(sketch, "E191.MirrorC", {"center": v(-25.55, 21.5) * mm, "radius": 0.5 * mm});
            skCircle(sketch, "E192.MirrorC", {"center": v(-14.05, 6.5) * mm, "radius": 0.5 * mm});
            skCircle(sketch, "E193.MirrorC", {"center": v(-14.05, 4) * mm, "radius": 0.5 * mm});
            skCircle(sketch, "E194.MirrorC", {"center": v(3.45, 9) * mm, "radius": 0.5 * mm});
            skCircle(sketch, "E195.MirrorC", {"center": v(31.95, 21.5) * mm, "radius": 0.5 * mm});
            skCircle(sketch, "E196.MirrorC", {"center": v(10.95, 6.5) * mm, "radius": 0.5 * mm});
            skCircle(sketch, "E197.MirrorC", {"center": v(18.45, 6.5) * mm, "radius": 0.5 * mm});
            skCircle(sketch, "E198.MirrorC", {"center": v(-29.05, 11.5) * mm, "radius": 0.5 * mm});
            skCircle(sketch, "E199.MirrorC", {"center": v(28.45, 4) * mm, "radius": 0.5 * mm});
            skCircle(sketch, "E200.MirrorC", {"center": v(14.45, 21.5) * mm, "radius": 0.5 * mm});
            skCircle(sketch, "E201.MirrorC", {"center": v(-15.55, 21.5) * mm, "radius": 0.5 * mm});
            skCircle(sketch, "E202.MirrorC", {"center": v(10.95, 4) * mm, "radius": 0.5 * mm});
            skCircle(sketch, "E203.MirrorC", {"center": v(33.45, 4) * mm, "radius": 0.5 * mm});
            skCircle(sketch, "E204.MirrorC", {"center": v(-9.05, 6.5) * mm, "radius": 0.5 * mm});
            skCircle(sketch, "E205.MirrorC", {"center": v(10.95, 9) * mm, "radius": 0.5 * mm});
            skCircle(sketch, "E206.MirrorC", {"center": v(15.95, 4) * mm, "radius": 0.5 * mm});
            skCircle(sketch, "E207.MirrorC", {"center": v(-14.05, 14) * mm, "radius": 0.5 * mm});
            skCircle(sketch, "E208.MirrorC", {"center": v(23.45, 14) * mm, "radius": 0.5 * mm});
            skCircle(sketch, "E209.MirrorC", {"center": v(-29.05, 14) * mm, "radius": 0.5 * mm});
            skCircle(sketch, "E210.MirrorC", {"center": v(20.95, 6.5) * mm, "radius": 0.5 * mm});
            skCircle(sketch, "E211.MirrorC", {"center": v(-21.55, 11.5) * mm, "radius": 0.5 * mm});
            skCircle(sketch, "E212.MirrorC", {"center": v(-11.55, 9) * mm, "radius": 0.5 * mm});
            skCircle(sketch, "E213.MirrorC", {"center": v(1.95, 24) * mm, "radius": 0.5 * mm});
            skCircle(sketch, "E214.MirrorC", {"center": v(23.45, 11.5) * mm, "radius": 0.5 * mm});
            skCircle(sketch, "E215.MirrorC", {"center": v(-3.05, 24) * mm, "radius": 0.5 * mm});
            skCircle(sketch, "E216.MirrorC", {"center": v(8.45, 9) * mm, "radius": 0.5 * mm});
            skCircle(sketch, "E217.MirrorC", {"center": v(25.95, 4) * mm, "radius": 0.5 * mm});
            skCircle(sketch, "E218.MirrorC", {"center": v(34.45, 21.5) * mm, "radius": 0.5 * mm});
            skCircle(sketch, "E219.MirrorC", {"center": v(-16.55, 6.5) * mm, "radius": 0.5 * mm});
            skCircle(sketch, "E220.MirrorC", {"center": v(20.95, 4) * mm, "radius": 0.5 * mm});
            skCircle(sketch, "E221.MirrorC", {"center": v(26.95, 24) * mm, "radius": 0.5 * mm});
            skCircle(sketch, "E222.MirrorC", {"center": v(0.95, 6.5) * mm, "radius": 0.5 * mm});
            skCircle(sketch, "E223.MirrorC", {"center": v(11.95, 24) * mm, "radius": 0.5 * mm});
            skCircle(sketch, "E224.MirrorC", {"center": v(4.45, 24) * mm, "radius": 0.5 * mm});
            skCircle(sketch, "E225.MirrorC", {"center": v(30.95, 6.5) * mm, "radius": 0.5 * mm});
            skCircle(sketch, "E226.MirrorC", {"center": v(-31.55, 11.5) * mm, "radius": 0.5 * mm});
            skCircle(sketch, "E227.MirrorC", {"center": v(-15.55, 24) * mm, "radius": 0.5 * mm});
            skLineSegment(sketch, "E228.MirrorCS", {"start": v(-42.05, 18.25) * mm, "end": v(42.05, 18.25) * mm});
            skLineSegment(sketch, "E229.MirrorCS", {"start": v(-42.05, 17.75) * mm, "end": v(42.05, 17.75) * mm});
            skLineSegment(sketch, "E230.MirrorCS", {"start": v(-36.55, 4) * mm, "end": v(-11.55, 4) * mm, "construction": true});
            skLineSegment(sketch, "E231.MirrorCS", {"start": v(-35.55, 21.5) * mm, "end": v(-33.05, 21.5) * mm, "construction": true});
            skLineSegment(sketch, "E232.MirrorCS", {"start": v(9.45, 21.5) * mm, "end": v(11.95, 21.5) * mm, "construction": true});
            skLineSegment(sketch, "E233.MirrorCS", {"start": v(9.45, 21.5) * mm, "end": v(9.45, 24) * mm, "construction": true});
            skLineSegment(sketch, "E234.MirrorCS", {"start": v(-20.55, 21.5) * mm, "end": v(-20.55, 24) * mm, "construction": true});
            skLineSegment(sketch, "E235.MirrorCS", {"start": v(-35.55, 21.5) * mm, "end": v(-35.55, 24) * mm, "construction": true});
            skLineSegment(sketch, "E236.MirrorCS", {"start": v(24.45, 21.5) * mm, "end": v(26.95, 21.5) * mm, "construction": true});
            skLineSegment(sketch, "E237.MirrorCS", {"start": v(-5.55, 21.5) * mm, "end": v(-3.05, 21.5) * mm, "construction": true});
            skLineSegment(sketch, "E238.MirrorCS", {"start": v(-20.55, 21.5) * mm, "end": v(-18.05, 21.5) * mm, "construction": true});
            skLineSegment(sketch, "E239.MirrorCS", {"start": v(24.45, 21.5) * mm, "end": v(24.45, 24) * mm, "construction": true});
            skLineSegment(sketch, "E240.MirrorCS", {"start": v(-5.55, 21.5) * mm, "end": v(-5.55, 24) * mm, "construction": true});
            skLineSegment(sketch, "E241.MirrorCS", {"start": v(-35.55, 24) * mm, "end": v(-20.55, 24) * mm, "construction": true});
            skSolve(sketch);
        }
        {
            var Q0;
            Q0 = qSketchRegion(id + "F5", true);
            extrude(context, id + "F6", {"entities" : qUnion([Q0]), "operationType" : NewBodyOperationType.REMOVE, "oppositeDirection" : true, "depth" : 4 * mm, "offsetDistance" : 25 * mm});
        }
    });
